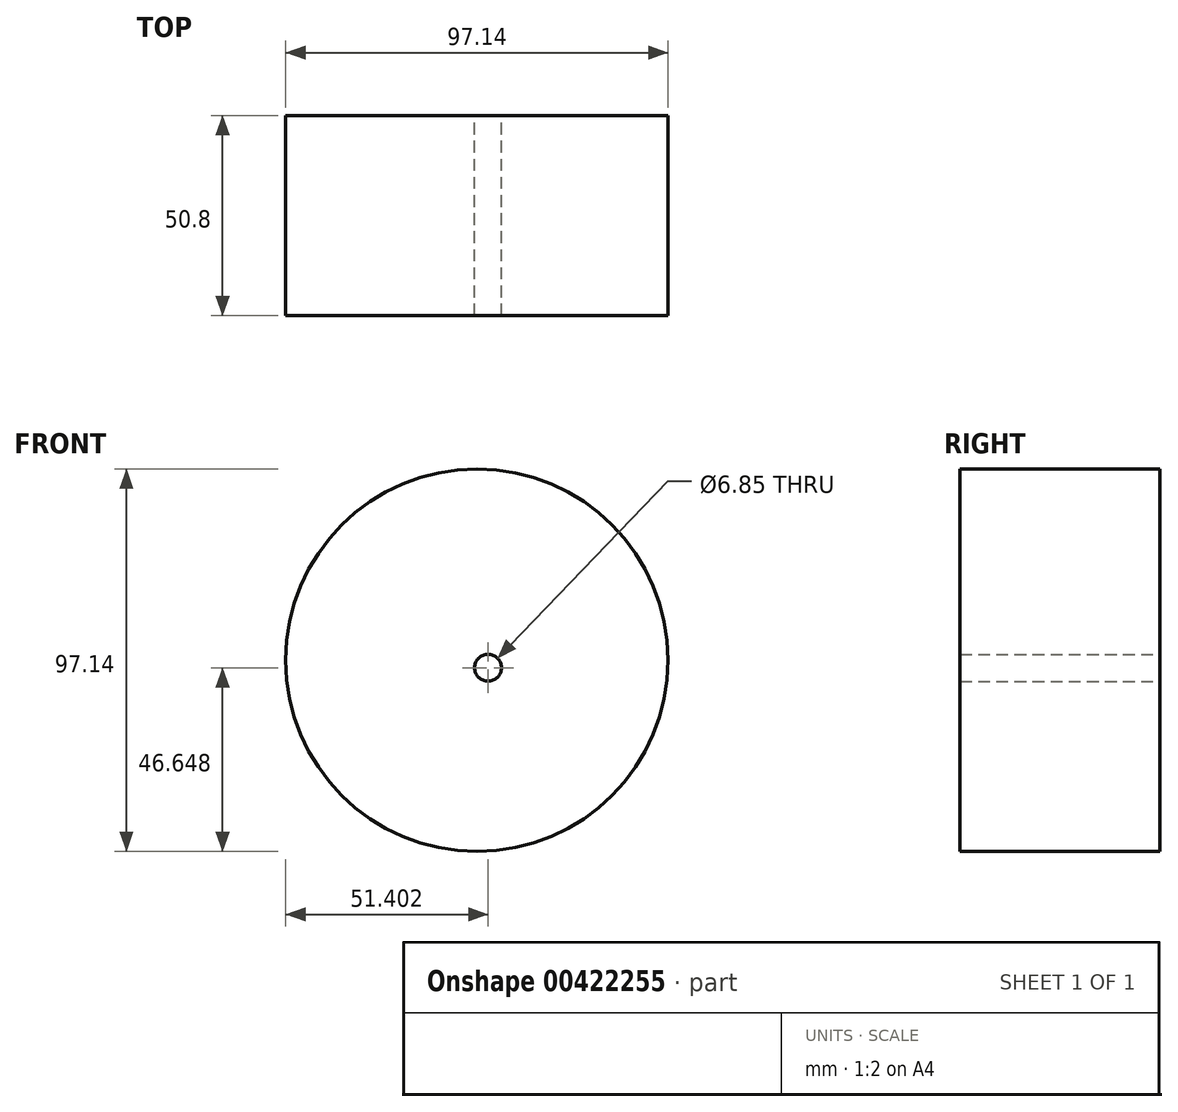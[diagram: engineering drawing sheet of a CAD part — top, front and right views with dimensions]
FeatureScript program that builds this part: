
annotation { "Feature Type Name" : "Feature", "Feature Type Description" : "" }
export const myFeature = defineFeature(function(context is Context, id is Id, definition is map)
    precondition{}
    {
        {
            var Q0;
            Q0=qCreatedBy(makeId("Front.planeOp"),FACE);
            var sketch = newSketch(context, id + "F0", { "sketchPlane" : qUnion([Q0])});
            skCircle(sketch, "E0", {"center": v(2.83, -1.92) * mm, "radius": 3.42 * mm});
            skCircle(sketch, "E1", {"center": v(0, 0) * mm, "radius": 48.57 * mm});
            skSolve(sketch);
        }
        {
            var Q0;
            Q0 = qSketchRegion(id + "F0", true);
            extrude(context, id + "F1", {"entities" : qUnion([Q0]), "depth" : 50.8 * mm});
        }
    });
